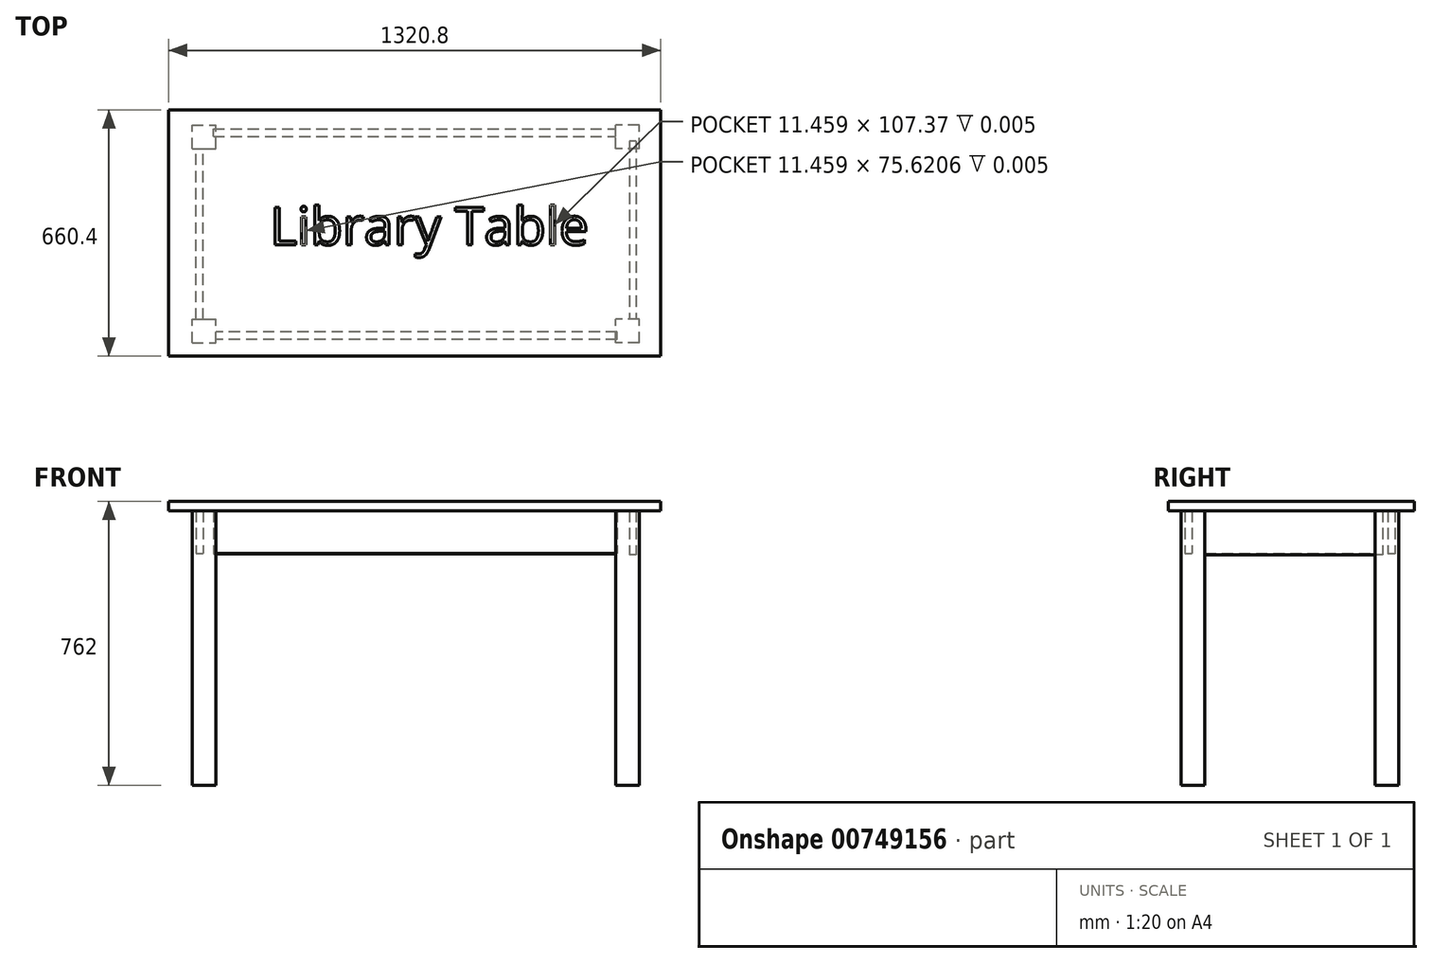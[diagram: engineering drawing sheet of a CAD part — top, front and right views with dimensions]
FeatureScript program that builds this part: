
annotation { "Feature Type Name" : "Feature", "Feature Type Description" : "" }
export const myFeature = defineFeature(function(context is Context, id is Id, definition is map)
    precondition{}
    {
        {
            var Q0;
            Q0=qCreatedBy(makeId("Top.planeOp"),FACE);
            var sketch = newSketch(context, id + "F0", { "sketchPlane" : qUnion([Q0])});
            skLineSegment(sketch, "E0.bottom", {"start": v(0, 0) * mm, "end": v(63.5, 0) * mm});
            skLineSegment(sketch, "E0.top", {"start": v(0, 63.5) * mm, "end": v(63.5, 63.5) * mm});
            skLineSegment(sketch, "E0.left", {"start": v(0, 0) * mm, "end": v(0, 63.5) * mm});
            skLineSegment(sketch, "E0.right", {"start": v(63.5, 0) * mm, "end": v(63.5, 63.5) * mm});
            skLineSegment(sketch, "E1.bottom", {"start": v(1200.15, 0) * mm, "end": v(1136.65, 0) * mm});
            skLineSegment(sketch, "E1.top", {"start": v(1200.15, 63.5) * mm, "end": v(1136.65, 63.5) * mm});
            skLineSegment(sketch, "E1.left", {"start": v(1200.15, 0) * mm, "end": v(1200.15, 63.5) * mm});
            skLineSegment(sketch, "E1.right", {"start": v(1136.65, 0) * mm, "end": v(1136.65, 63.5) * mm});
            skLineSegment(sketch, "E2.bottom", {"start": v(0, 520.7) * mm, "end": v(63.5, 520.7) * mm});
            skLineSegment(sketch, "E2.top", {"start": v(0, 584.2) * mm, "end": v(63.5, 584.2) * mm});
            skLineSegment(sketch, "E2.left", {"start": v(0, 520.7) * mm, "end": v(0, 584.2) * mm});
            skLineSegment(sketch, "E2.right", {"start": v(63.5, 520.7) * mm, "end": v(63.5, 584.2) * mm});
            skLineSegment(sketch, "E3.bottom", {"start": v(1200.15, 520.7) * mm, "end": v(1136.65, 520.7) * mm});
            skLineSegment(sketch, "E3.top", {"start": v(1200.15, 584.2) * mm, "end": v(1136.65, 584.2) * mm});
            skLineSegment(sketch, "E3.left", {"start": v(1200.15, 520.7) * mm, "end": v(1200.15, 584.2) * mm});
            skLineSegment(sketch, "E3.right", {"start": v(1136.65, 520.7) * mm, "end": v(1136.65, 584.2) * mm});
            skSolve(sketch);
        }
        {
            var Q0;
            Q0 = qSketchRegion(id + "F0", true);
            extrude(context, id + "F1", {"entities" : qUnion([Q0]), "depth" : 736.6 * mm, "offsetDistance" : 25.4 * mm});
        }
        {
            var Q0;
            Q0=makeQuery(id+"F1.opExtrude","CAP_FACE",FACE,{"disambiguationData":[OSD([sQuery(id+"F0.wireOp",EDGE,"E0.bottom"),sQuery(id+"F0.wireOp",EDGE,"E0.top"),sQuery(id+"F0.wireOp",EDGE,"E0.left"),sQuery(id+"F0.wireOp",EDGE,"E0.right")])],"isStart":false});
            var sketch = newSketch(context, id + "F2", { "sketchPlane" : qUnion([Q0])});
            skLineSegment(sketch, "E4.bottom", {"start": v(-63.5, 625.35) * mm, "end": v(1257.3, 625.35) * mm});
            skLineSegment(sketch, "E4.top", {"start": v(-63.5, -35.05) * mm, "end": v(1257.3, -35.05) * mm});
            skLineSegment(sketch, "E4.left", {"start": v(-63.5, 625.35) * mm, "end": v(-63.5, -35.05) * mm});
            skLineSegment(sketch, "E4.right", {"start": v(1257.3, 625.35) * mm, "end": v(1257.3, -35.05) * mm});
            skSolve(sketch);
        }
        {
            var Q0;
            Q0 = qSketchRegion(id + "F2", true);
            extrude(context, id + "F3", {"entities" : qUnion([Q0]), "depth" : 25.4 * mm, "offsetDistance" : 25.4 * mm});
        }
        {
            var Q0;
            Q0=makeQuery(id+"F1.opExtrude","SWEPT_FACE",FACE,{"disambiguationData":[OSD([sQuery(id+"F0.wireOp",EDGE,"E0.right")])]});
            var sketch = newSketch(context, id + "F4", { "sketchPlane" : qUnion([Q0])});
            skLineSegment(sketch, "E5.bottom", {"start": v(9.66, 736.6) * mm, "end": v(29.32, 736.6) * mm});
            skLineSegment(sketch, "E5.top", {"start": v(9.66, 621.81) * mm, "end": v(29.32, 621.81) * mm});
            skLineSegment(sketch, "E5.left", {"start": v(9.66, 736.6) * mm, "end": v(9.66, 621.81) * mm});
            skLineSegment(sketch, "E5.right", {"start": v(29.32, 736.6) * mm, "end": v(29.32, 621.81) * mm});
            skSolve(sketch);
        }
        {
            var Q0;
            Q0 = qSketchRegion(id + "F4", true);
            extrude(context, id + "F5", {"entities" : qUnion([Q0]), "depth" : 1076.96 * mm, "offsetDistance" : 25.4 * mm});
        }
        {
            var Q0;
            Q0=makeQuery(id+"F1.opExtrude","SWEPT_FACE",FACE,{"disambiguationData":[OSD([sQuery(id+"F0.wireOp",EDGE,"E2.bottom")])]});
            var sketch = newSketch(context, id + "F6", { "sketchPlane" : qUnion([Q0])});
            skLineSegment(sketch, "E6.bottom", {"start": v(10.57, 736.6) * mm, "end": v(29.82, 736.6) * mm});
            skLineSegment(sketch, "E6.top", {"start": v(10.57, 622.57) * mm, "end": v(29.82, 622.57) * mm});
            skLineSegment(sketch, "E6.left", {"start": v(10.57, 736.6) * mm, "end": v(10.57, 622.57) * mm});
            skLineSegment(sketch, "E6.right", {"start": v(29.82, 736.6) * mm, "end": v(29.82, 622.57) * mm});
            skSolve(sketch);
        }
        {
            var Q0;
            Q0 = qSketchRegion(id + "F6", true);
            extrude(context, id + "F7", {"entities" : qUnion([Q0]), "operationType" : NewBodyOperationType.ADD, "depth" : 469.4 * mm, "offsetDistance" : 25.4 * mm});
        }
        {
            var Q0;
            Q0=makeQuery(id+"F1.opExtrude","SWEPT_FACE",FACE,{"disambiguationData":[OSD([sQuery(id+"F0.wireOp",EDGE,"E3.right")])]});
            var sketch = newSketch(context, id + "F8", { "sketchPlane" : qUnion([Q0])});
            skLineSegment(sketch, "E7.bottom", {"start": v(-574.29, 736.6) * mm, "end": v(-554.85, 736.6) * mm});
            skLineSegment(sketch, "E7.top", {"start": v(-574.29, 621.42) * mm, "end": v(-554.85, 621.42) * mm});
            skLineSegment(sketch, "E7.left", {"start": v(-574.29, 736.6) * mm, "end": v(-574.29, 621.42) * mm});
            skLineSegment(sketch, "E7.right", {"start": v(-554.85, 736.6) * mm, "end": v(-554.85, 621.42) * mm});
            skSolve(sketch);
        }
        {
            var Q0;
            Q0 = qSketchRegion(id + "F8", true);
            extrude(context, id + "F9", {"entities" : qUnion([Q0]), "depth" : 1079.5 * mm, "offsetDistance" : 25.4 * mm});
        }
        {
            var Q0;
            Q0=makeQuery(id+"F1.opExtrude","SWEPT_FACE",FACE,{"disambiguationData":[OSD([sQuery(id+"F0.wireOp",EDGE,"E1.top")])]});
            var sketch = newSketch(context, id + "F10", { "sketchPlane" : qUnion([Q0])});
            skLineSegment(sketch, "E8.bottom", {"start": v(-1191.16, 736.6) * mm, "end": v(-1173.25, 736.6) * mm});
            skLineSegment(sketch, "E8.top", {"start": v(-1191.16, 618.68) * mm, "end": v(-1173.25, 618.68) * mm});
            skLineSegment(sketch, "E8.left", {"start": v(-1191.16, 736.6) * mm, "end": v(-1191.16, 618.68) * mm});
            skLineSegment(sketch, "E8.right", {"start": v(-1173.25, 736.6) * mm, "end": v(-1173.25, 618.68) * mm});
            skSolve(sketch);
        }
        {
            var Q0;
            Q0 = qSketchRegion(id + "F10", true);
            extrude(context, id + "F11", {"entities" : qUnion([Q0]), "depth" : 477.52 * mm, "offsetDistance" : 25.4 * mm});
        }
        {
            var Q0;
            Q0=makeQuery(id+"F3.opExtrude","CAP_FACE",FACE,{"disambiguationData":[OSD([sQuery(id+"F2.wireOp",EDGE,"E4.bottom"),sQuery(id+"F2.wireOp",EDGE,"E4.top"),sQuery(id+"F2.wireOp",EDGE,"E4.left"),sQuery(id+"F2.wireOp",EDGE,"E4.right")])],"isStart":false});
            var sketch = newSketch(context, id + "F12", { "sketchPlane" : qUnion([Q0])});
            skText(sketch, "E9", { "text": "Library Table", "fontName": "OpenSans-Regular.ttf"});
            const initialGuessF12  = {"E9": [0.20806, 0.26325, 1, 0, 0.10174]};
            skSetInitialGuess(sketch, initialGuessF12);
            skSolve(sketch);
        }
        {
            var Q0;
            Q0 = qSketchRegion(id + "F12", true);
            extrude(context, id + "F13", {"entities" : qUnion([Q0]), "operationType" : NewBodyOperationType.REMOVE, "oppositeDirection" : true, "depth" : 1 / 203.2 * mm, "offsetDistance" : 25.4 * mm});
        }
    });
